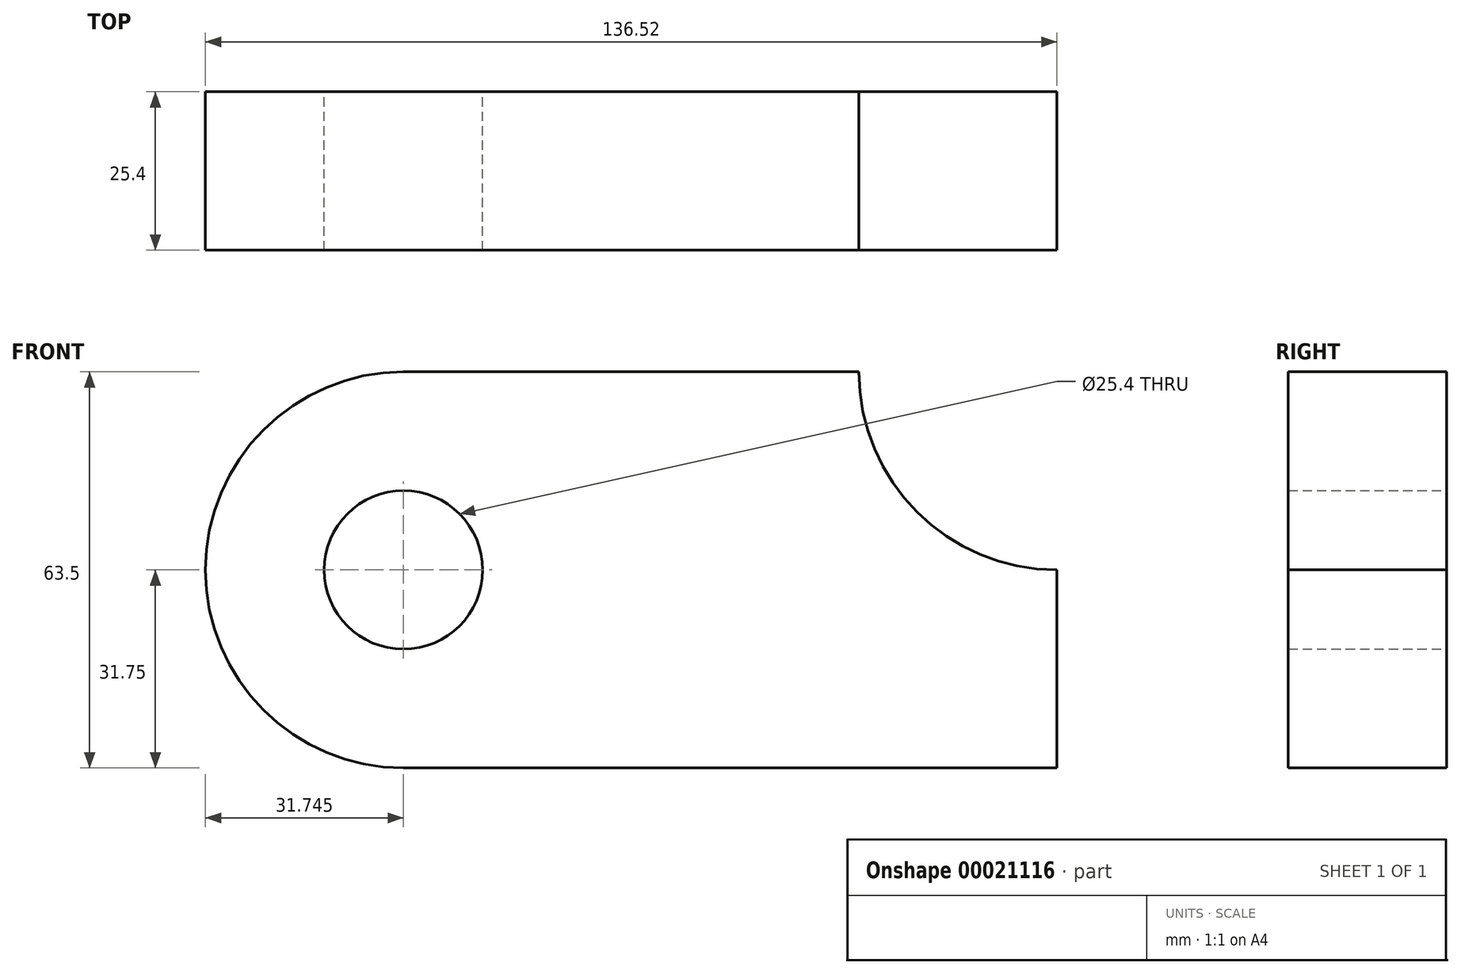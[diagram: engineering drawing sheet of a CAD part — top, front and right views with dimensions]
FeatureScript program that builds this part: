
annotation { "Feature Type Name" : "Feature", "Feature Type Description" : "" }
export const myFeature = defineFeature(function(context is Context, id is Id, definition is map)
    precondition{}
    {
        {
            var Q0;
            Q0=qCreatedBy(makeId("Front.planeOp"),FACE);
            var sketch = newSketch(context, id + "F0", { "sketchPlane" : qUnion([Q0])});
            skLineSegment(sketch, "E0.bottom", {"start": v(-104.78, 63.5) * mm, "end": v(0, 63.5) * mm});
            skLineSegment(sketch, "E0.top", {"start": v(-104.78, 0) * mm, "end": v(0, 0) * mm});
            skLineSegment(sketch, "E0.left", {"start": v(-104.78, 63.5) * mm, "end": v(-104.78, 0) * mm});
            skLineSegment(sketch, "E0.right", {"start": v(0, 63.5) * mm, "end": v(0, 0) * mm});
            skCircle(sketch, "E1", {"center": v(-104.78, 31.75) * mm, "radius": 31.75 * mm});
            skCircle(sketch, "E2", {"center": v(-104.78, 31.75) * mm, "radius": 12.7 * mm});
            skCircle(sketch, "E3", {"center": v(0, 63.5) * mm, "radius": 31.75 * mm});
            skSolve(sketch);
        }
        {
            var Q0;
            {var subQ6=sQuery(id+"F0.wireOp",EDGE,"E0.top");Q0=makeQuery(id+"F0.imprint","IMPRINT",FACE,{"disambiguationData":[TD([[makeQuery(id+"F0.imprint","IMPRINT",EDGE,{"derivedFrom":subQ6}),1.0]])]});}
            var Q1;
            {var subQ0=sQuery(id+"F0.wireOp",EDGE,"E2");var subQ1=sQuery(id+"F0.wireOp",EDGE,"E0.left");var subQ3=makeQuery(id+"F0.imprint","INTERSECT",VERTEX,{"disambiguationData":[OD(0.0)],"derivedFrom":[subQ1,subQ0]});Q1=makeQuery(id+"F0.imprint","IMPRINT",FACE,{"disambiguationData":[TD([[makeQuery(id+"F0.imprint","IMPRINT",EDGE,{"disambiguationData":[TD([[subQ3,-1.0]])],"derivedFrom":subQ0}),-1.0]])]});}
            var Q2;
            {var subQ0=sQuery(id+"F0.wireOp",EDGE,"E2");var subQ1=sQuery(id+"F0.wireOp",EDGE,"E0.left");var subQ3=makeQuery(id+"F0.imprint","INTERSECT",VERTEX,{"disambiguationData":[OD(0.0)],"derivedFrom":[subQ1,subQ0]});Q2=makeQuery(id+"F0.imprint","IMPRINT",FACE,{"disambiguationData":[TD([[makeQuery(id+"F0.imprint","IMPRINT",EDGE,{"disambiguationData":[TD([[subQ3,1.0]])],"derivedFrom":subQ0}),-1.0]])]});}
            extrude(context, id + "F1", {"entities" : qUnion([Q0, Q1, Q2]), "depth" : 25.4 * mm});
        }
    });
